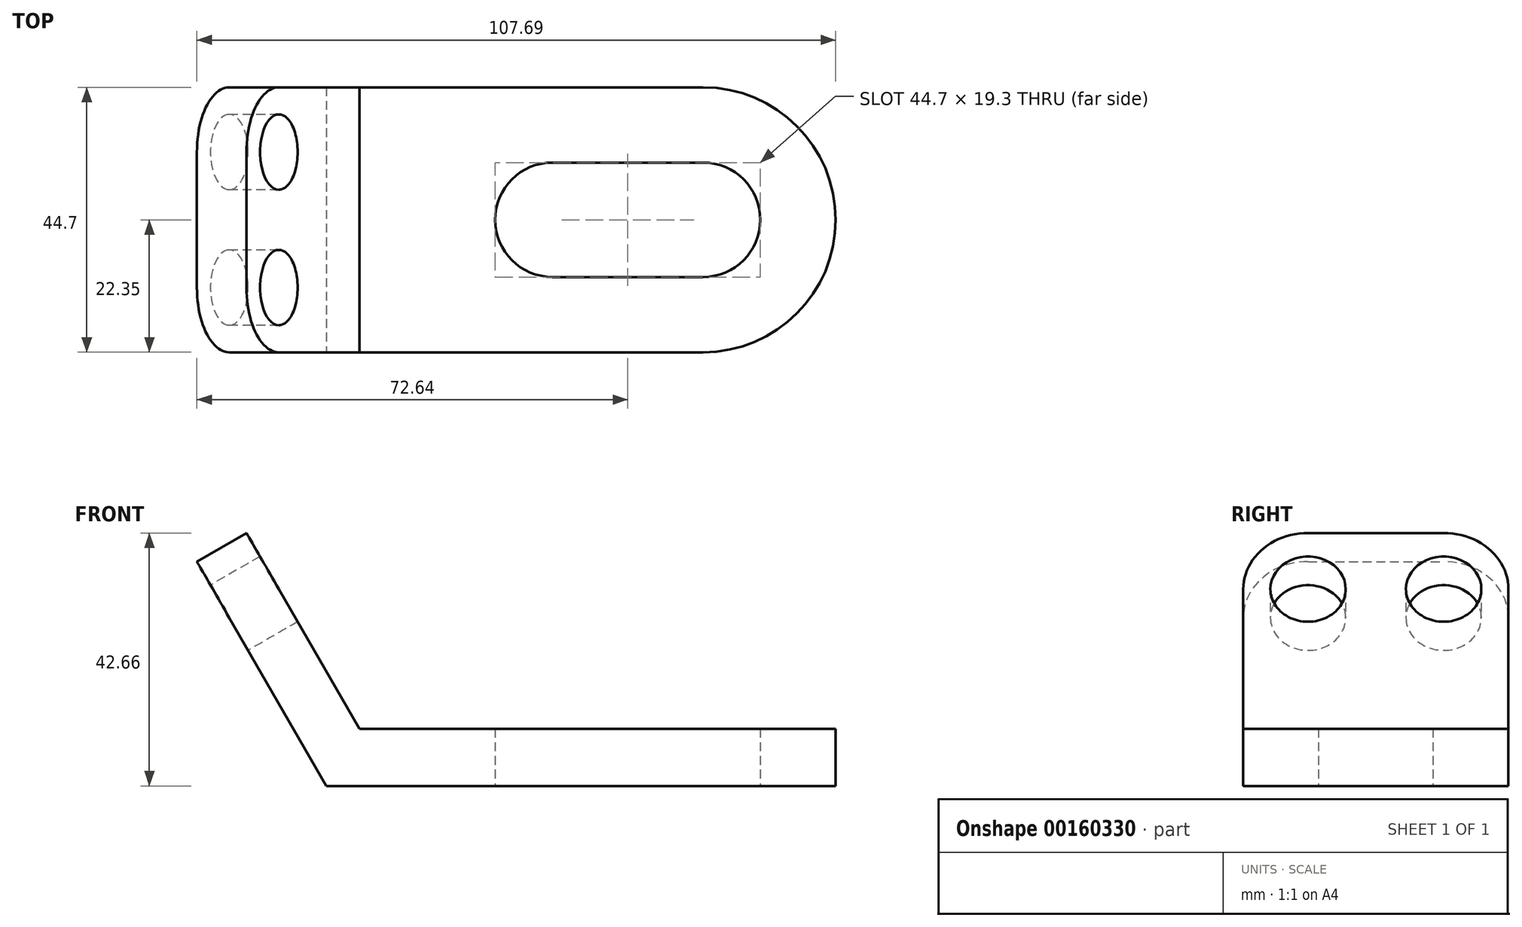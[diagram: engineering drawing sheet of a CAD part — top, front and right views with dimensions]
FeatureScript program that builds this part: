
annotation { "Feature Type Name" : "Feature", "Feature Type Description" : "" }
export const myFeature = defineFeature(function(context is Context, id is Id, definition is map)
    precondition{}
    {
        {
            var Q0;
            Q0=qCreatedBy(makeId("Top.planeOp"),FACE);
            var sketch = newSketch(context, id + "F0", { "sketchPlane" : qUnion([Q0])});
            skArc(sketch, "E0", {"start": v(0, -9.65) * mm, "mid": v(9.65, 0) * mm, "end": v(0, 9.65) * mm});
            skArc(sketch, "E1", {"start": v(-25.4, 9.65) * mm, "mid": v(-35.05, 0) * mm, "end": v(-25.4, -9.65) * mm});
            skLineSegment(sketch, "E2", {"start": v(-25.4, 9.65) * mm, "end": v(0, 9.65) * mm});
            skLineSegment(sketch, "E3", {"start": v(-25.4, -9.65) * mm, "end": v(0, -9.65) * mm});
            skArc(sketch, "E4", {"start": v(0, -22.35) * mm, "mid": v(22.35, 0) * mm, "end": v(0, 22.35) * mm});
            skLineSegment(sketch, "E5", {"start": v(0, 22.35) * mm, "end": v(-63.5, 22.35) * mm});
            skLineSegment(sketch, "E6", {"start": v(-63.5, 22.35) * mm, "end": v(-63.5, -22.35) * mm});
            skLineSegment(sketch, "E7", {"start": v(-63.5, -22.35) * mm, "end": v(0, -22.35) * mm});
            skSolve(sketch);
        }
        {
            var Q0;
            Q0=sQuery(id+"F0.wireOp",EDGE,"E6");
            cPlane(context, id + "F1", {"entities" : qUnion([Q0]), "cplaneType" : CPlaneType.LINE_ANGLE, "offset" : 25.4 * mm, "angle" : 120 * degree, "width" : 152.4 * mm, "height" : 152.4 * mm});
        }
        {
            var Q0;
            Q0=qCreatedBy(id+"F1.planeOp",FACE);
            var sketch = newSketch(context, id + "F2", { "sketchPlane" : qUnion([Q0])});
            skLineSegment(sketch, "E8.0", {"start": v(22.35, 31.75) * mm, "end": v(-22.35, 31.75) * mm});
            skLineSegment(sketch, "E9", {"start": v(-22.35, 31.75) * mm, "end": v(-22.35, 64.52) * mm});
            skLineSegment(sketch, "E10", {"start": v(-11.43, 75.44) * mm, "end": v(11.43, 75.44) * mm});
            skLineSegment(sketch, "E11", {"start": v(22.35, 64.52) * mm, "end": v(22.35, 31.75) * mm});
            skPoint(sketch, "E12.visualSharp", {"position": v(-22.35, 75.44) * mm});
            skArc(sketch, "E12.filletArc", {"start": v(-11.43, 75.44) * mm, "mid": v(-19.15, 72.24) * mm, "end": v(-22.35, 64.52) * mm});
            skPoint(sketch, "E13.visualSharp", {"position": v(22.35, 75.44) * mm});
            skArc(sketch, "E13.filletArc", {"start": v(22.35, 64.52) * mm, "mid": v(19.15, 72.24) * mm, "end": v(11.43, 75.44) * mm});
            skCircle(sketch, "E14", {"center": v(-11.43, 64.52) * mm, "radius": 6.35 * mm});
            skCircle(sketch, "E15", {"center": v(11.43, 64.52) * mm, "radius": 6.35 * mm});
            skCircle(sketch, "E16", {"center": v(11.43, 64.52) * mm, "radius": 3.18 * mm});
            skCircle(sketch, "E17", {"center": v(-11.43, 64.52) * mm, "radius": 3.18 * mm});
            skSolve(sketch);
        }
        {
            var Q0;
            Q0=makeQuery(id+"F2.imprint","IMPRINT",FACE,{"disambiguationData":[TD([[makeQuery(id+"F2.imprint","IMPRINT",EDGE,{"derivedFrom":sQuery(id+"F2.wireOp",EDGE,"E8.0")}),-1.0]])]});
            extrude(context, id + "F3", {"entities" : qUnion([Q0]), "depth" : 9.65 * mm});
        }
        {
            var Q0;
            Q0=makeQuery(id+"F0.imprint","IMPRINT",FACE,{"disambiguationData":[TD([[makeQuery(id+"F0.imprint","IMPRINT",EDGE,{"derivedFrom":sQuery(id+"F0.wireOp",EDGE,"E0")}),-1.0]])]});
            extrude(context, id + "F4", {"entities" : qUnion([Q0]), "operationType" : NewBodyOperationType.ADD, "depth" : 9.65 * mm});
        }
    });
